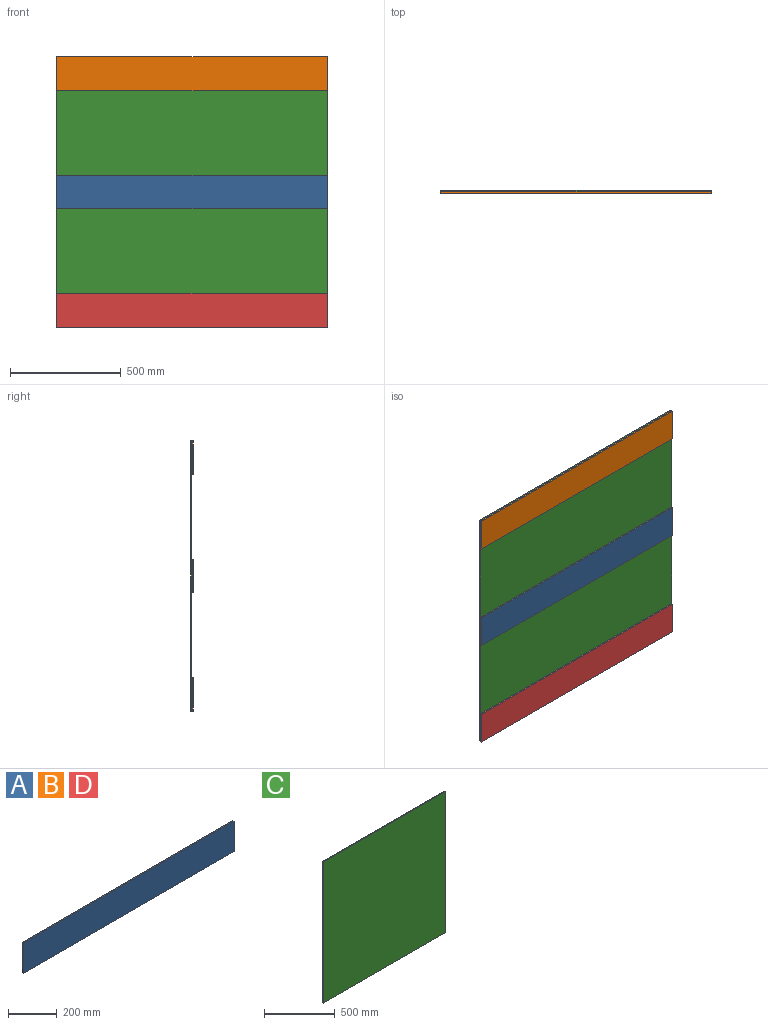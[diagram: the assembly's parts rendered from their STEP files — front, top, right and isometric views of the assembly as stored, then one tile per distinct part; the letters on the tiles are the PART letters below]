
ASSEMBLY  parts=4 mates=3
PART A: 6 faces, bbox 1219.2x6.4x152.4 mm
  f0: plane 152.4x6.35mm, normal (-1,0,0), area 967.7mm2, adj f1,f3,f4,f5
  f1: plane 1219.2x6.35mm, normal (0,0,-1), area 7741.9mm2, adj f0,f2,f4,f5
  f2: plane 152.4x6.35mm, normal (1,0,0), area 967.7mm2, adj f1,f3,f4,f5
  f3: plane 1219.2x6.35mm, normal (0,0,1), area 7741.9mm2, adj f0,f2,f4,f5
  f4: plane 1219.2x152.4mm, normal (0,-1,0), area 185806.1mm2, adj f0,f1,f2,f3
  f5: plane 1219.2x152.4mm, normal (0,1,0), area 185806.1mm2, adj f0,f1,f2,f3
PART B: same geometry as A
PART C: 6 faces, bbox 1219.2x6.4x1219.2 mm
  f0: plane 1219.2x6.35mm, normal (-1,0,0), area 7741.9mm2, adj f1,f3,f4,f5
  f1: plane 1219.2x6.35mm, normal (0,0,-1), area 7741.9mm2, adj f0,f2,f4,f5
  f2: plane 1219.2x6.35mm, normal (1,0,0), area 7741.9mm2, adj f1,f3,f4,f5
  f3: plane 1219.2x6.35mm, normal (0,0,1), area 7741.9mm2, adj f0,f2,f4,f5
  f4: plane 1219.2x1219.2mm, normal (0,-1,0), area 1486448.6mm2, adj f0,f1,f2,f3
  f5: plane 1219.2x1219.2mm, normal (0,1,0), area 1486448.6mm2, adj f0,f1,f2,f3
PART D: same geometry as A
PLACE A t=(595.77,1446.55,633.76)mm
PLACE B t=(595.77,1446.55,1167.16)mm
PLACE C t=(595.77,1452.9,100.36)mm
PLACE D t=(595.77,1446.55,100.36)mm
MATE fastened D.f5 <-> C.f4  axis (0,1,0) through (1205.37,1446.55,176.56)mm
MATE fastened A.f5 <-> C.f4  axis (0,1,0) through (1205.37,1446.55,709.96)mm
MATE fastened B.f5 <-> C.f4  axis (0,1,0) through (1205.37,1446.55,1243.36)mm
